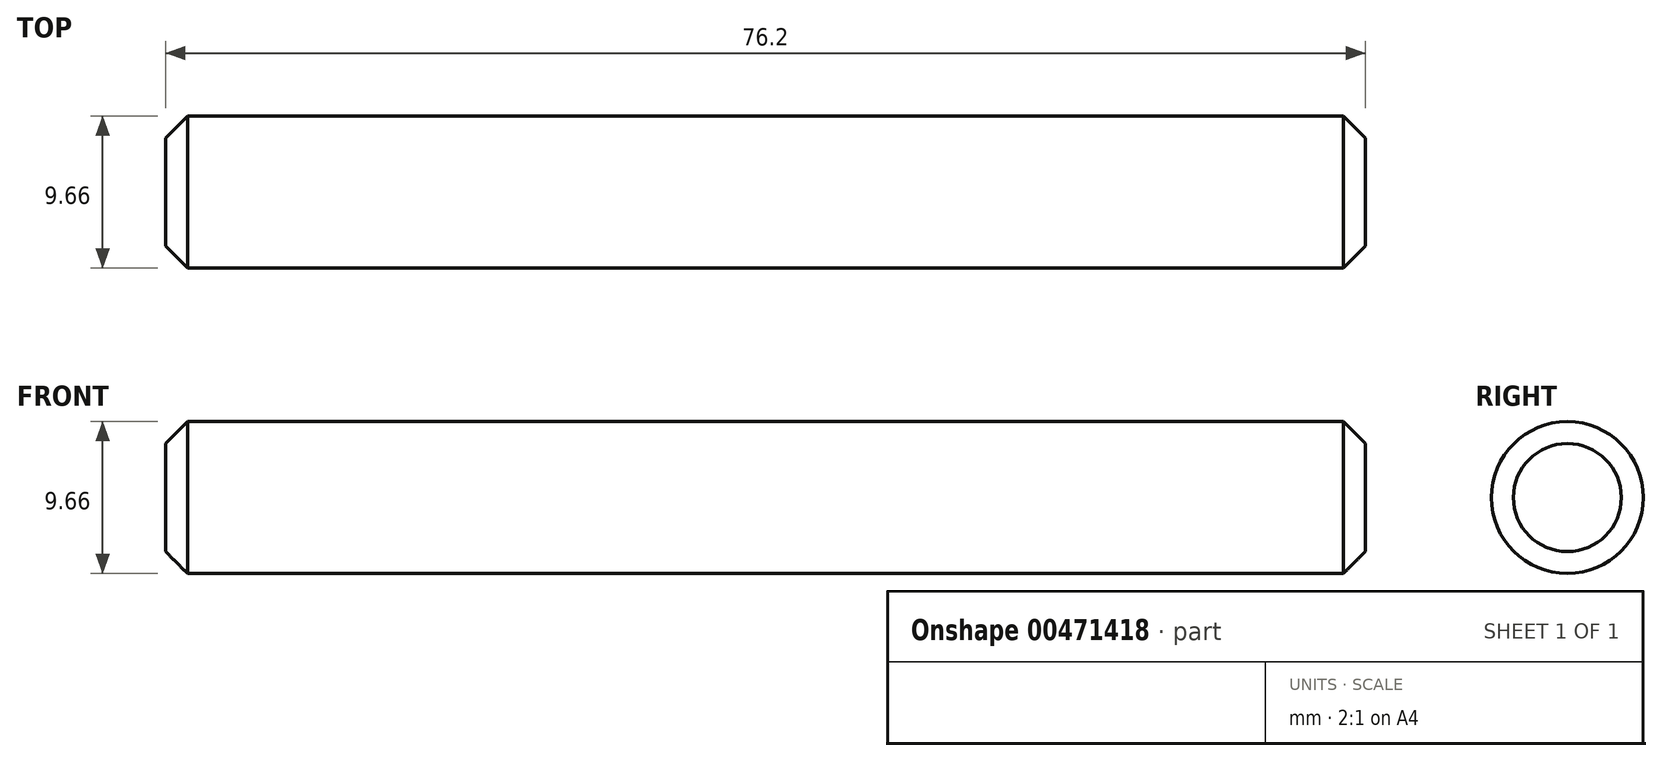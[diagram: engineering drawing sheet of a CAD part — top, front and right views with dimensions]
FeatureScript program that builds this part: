
annotation { "Feature Type Name" : "Feature", "Feature Type Description" : "" }
export const myFeature = defineFeature(function(context is Context, id is Id, definition is map)
    precondition{}
    {
        {
            var Q0;
            Q0=qCreatedBy(makeId("Front.planeOp"),FACE);
            var sketch = newSketch(context, id + "F0", { "sketchPlane" : qUnion([Q0])});
            skLineSegment(sketch, "E0.bottom", {"start": v(-76.2, 4.83) * mm, "end": v(0, 4.83) * mm});
            skLineSegment(sketch, "E0.top", {"start": v(-76.2, 0) * mm, "end": v(0, 0) * mm});
            skLineSegment(sketch, "E0.left", {"start": v(-76.2, 4.83) * mm, "end": v(-76.2, 0) * mm});
            skLineSegment(sketch, "E0.right", {"start": v(0, 4.83) * mm, "end": v(0, 0) * mm});
            skSolve(sketch);
        }
        {
            var Q0;
            Q0 = qSketchRegion(id + "F0", true);
            var Q1;
            Q1=sQuery(id+"F0.wireOp",EDGE,"E0.top");
            revolve(context, id + "F1", {"entities" : qUnion([Q0]), "axis" : qUnion([Q1]), "revolveType" : RevolveType.FULL});
        }
        {
            var Q0;
            Q0=makeQuery(id+"F1.opRevolve","SWEPT_EDGE",EDGE,{"disambiguationData":[OSD([sQuery(id+"F0.wireOp",EDGE,"E0.bottom"),sQuery(id+"F0.wireOp",EDGE,"E0.left")])]});
            var Q1;
            Q1=makeQuery(id+"F1.opRevolve","SWEPT_EDGE",EDGE,{"disambiguationData":[OSD([sQuery(id+"F0.wireOp",EDGE,"E0.bottom"),sQuery(id+"F0.wireOp",EDGE,"E0.right")])]});
            chamfer(context, id + "F2", {"entities" : qUnion([Q0, Q1]), "width" : 1.4 * mm, "tangentPropagation" : true});
        }
    });
